# Revit family: NBS_DuPontCorian_Snks_KitchenSink_Salty9410
name_source: partatom
category: Plumbing Fixtures
revit_build: Autodesk Revit 2014 (Build: 20130709_2115(x64)
units: mm (PartAtom-declared; Revit-internal decimal feet)

## types (1)
- 9410
    AccessibilityPerformance = http://www.dupont.co.uk
    AssetType = Fixed
    BIMObjectName = NBS_DuPontCorian_Sinks_KitchenSink_Salty9410
    BasinDepth = 195 mm  [stored 0.639764 ft]
    BasinLength = 850 mm  [stored 2.78871 ft]
    BasinWidth = 450 mm  [stored 1.47638 ft]
    Category = Pr_40_20_96_81 : Sinks
    Color = Glacier White, Designer White
    CounterVoidLength = 804 mm
    CounterVoidWidth = 404 mm
    DeclarationOfPerformance = CL 25 - EN 14688:2006
    Default Elevation = 0 mm  [stored 0 ft]
    Description = A flexible Corian(R) solid surface composite material double kitchen sink. Manufactured from natural minerals and acrylic resin. Designed to be seamlessly integrated into a Corian(R) surface.
    DrainSize = 46 mm
    DurationUnit = 40 years plus
    ExpectedLife = 40 years plus
    Features = Designed to be integrated into a Corian(R) surface. Available in the full colour range as standard or bespoke colours. Hygienic, easy to clean and maintain. Seamless joints.
    Finish = semi-gloss
    Form = Inset & integrated into surface or mounted under surface (undermount)
    IfcExportAs = IfcSanitaryTerminalType
    IfcExportType = SINK
    IntegralAccessories = Includes overflow piece & 25mm diameteroverflow elbow; drain cover
    InternalDepth = 176
    InternalLength = 800 (2 sections)
    InternalWidth = 400
    ManufacturerName = DuPont Corian
    ManufacturerURL = www.corian.co.uk
    Material = DuPont™ Corian® solid surface material
    ModelNumber = Salty 9410
    ModelReference = Salty 9410
    NBSCertification = http://www.nationalbimlibrary.com
    NBSDescription = Sinks
    NBSReference = 45-35-70/344
    Name = Sinks_KitchenSink_Salty9410_DuPontCorian
    NominalDepth = 195 mm  [stored 0.639764 ft]
    NominalHeight = 195 mm  [stored 0.639764 ft]
    NominalLength = 850 mm  [stored 2.78871 ft]
    NominalWidth = 450 mm  [stored 1.47638 ft]
    ProductInformation = www.dupont.co.uk/content/dam/dupont/products-and-services/construction-materials/surface-design-materials/documents/DuPont_Corian_Kitchen_and_Bathroom_Product_catalogue.pdf
    ReplacementCost = Repairable
    Shape = Double Rectangular
    SinkMaterial = NBS_Concept
    SinkMounting = Integrated into worksurface or mounted under (Undermount)
    SinkType = Kitchen
    Size = 800 x 400 x 176
    SustainabilityPerformance = ISO 14001. Zero landfill at manufacturing site. Greenguard certified. Repairable nature makes lifetime performance 40 years plus.
    TopCornerRadius = 10
    Uniclass2 = 45-31-79/415
    Uniclass2015Description = Sinks
    Uniclass2015Reference = Pr_40_20_96_81
    Uniclass2015Version = Products v1.1
    Version = 1
    WarrantyDescription = 10 year material warranty from DuPont(TM)
    WarrantyDurationParts = 10 years
    WasteOutletDiameter = 46 mm
    WaterSupplyOverflowAndWasteHolesOverflow = Round overflow hole with cover
    WaterSupplyOverflowAndWasteHolesWaste = No tapholes
    WaterSupplyOverflowAndWasteHolesWaterSupply = Round bottom waste outlet with drain cover

note: [stored X ft] marks values corroborated as IEEE doubles in the binary element streams (Revit-internal decimal feet)

## geometry (parser evidence)
native form markers: Sweep x5
no freeform markers — native parametric forms only
